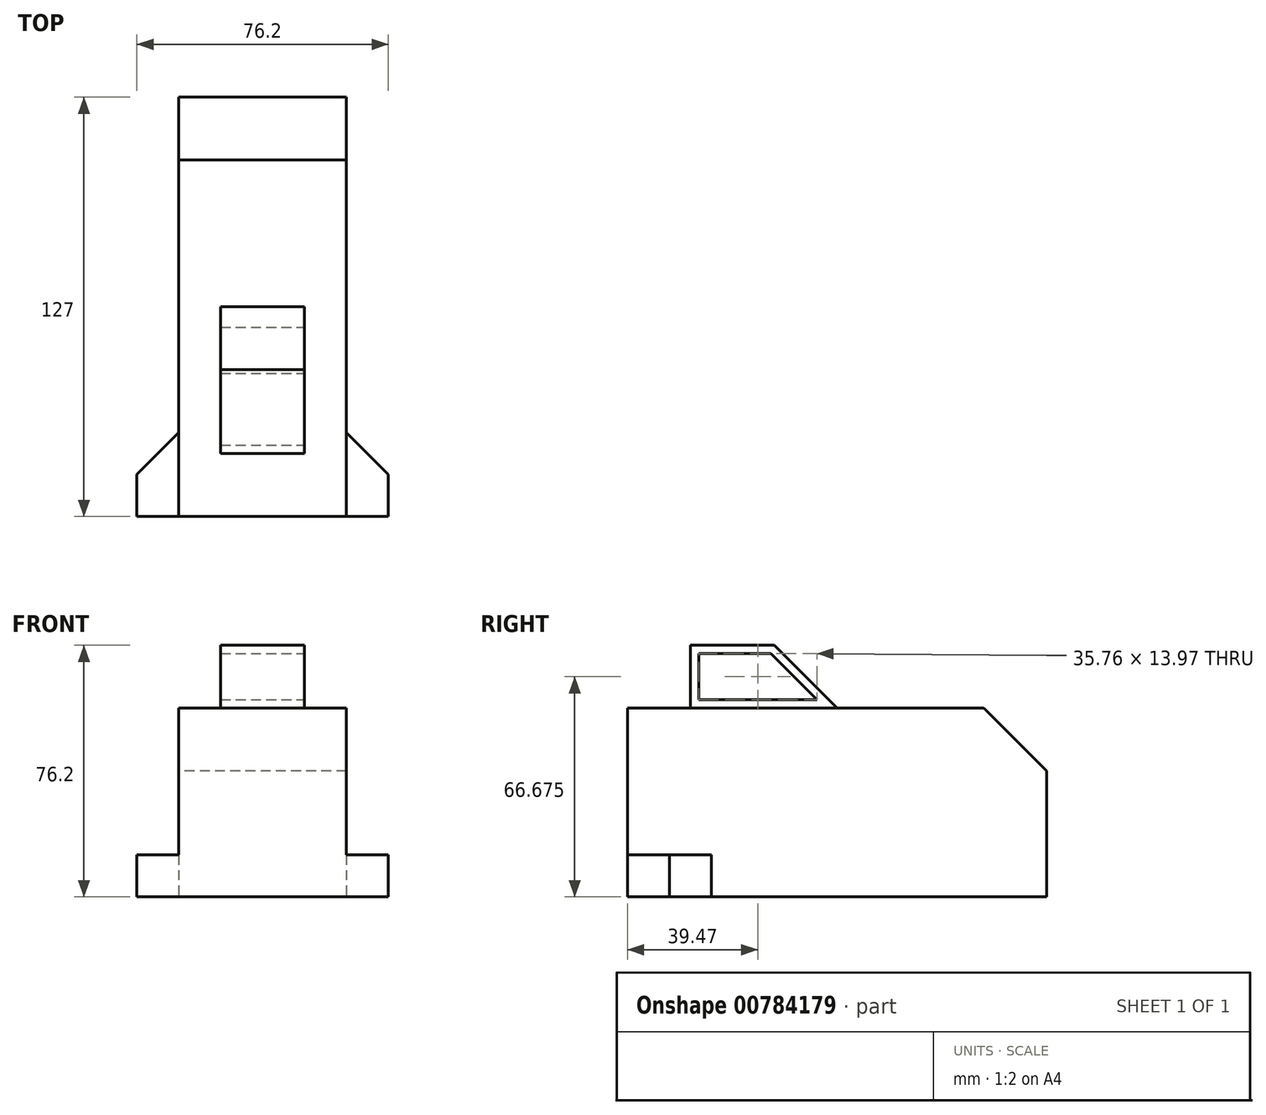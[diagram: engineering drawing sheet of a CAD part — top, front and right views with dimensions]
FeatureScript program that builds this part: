
annotation { "Feature Type Name" : "Feature", "Feature Type Description" : "" }
export const myFeature = defineFeature(function(context is Context, id is Id, definition is map)
    precondition{}
    {
        {
            var Q0;
            Q0=qCreatedBy(makeId("Right.planeOp"),FACE);
            var sketch = newSketch(context, id + "F0", { "sketchPlane" : qUnion([Q0])});
            skLineSegment(sketch, "E0", {"start": v(0, 0) * mm, "end": v(127, 0) * mm});
            skLineSegment(sketch, "E1", {"start": v(127, 0) * mm, "end": v(127, 38.1) * mm});
            skLineSegment(sketch, "E2", {"start": v(0, 0) * mm, "end": v(0, 57.15) * mm});
            skLineSegment(sketch, "E3", {"start": v(0, 57.15) * mm, "end": v(107.95, 57.15) * mm});
            skLineSegment(sketch, "E4", {"start": v(107.95, 57.15) * mm, "end": v(127, 38.1) * mm});
            skLineSegment(sketch, "E5", {"start": v(0, 0) * mm, "end": v(0, 12.7) * mm});
            skLineSegment(sketch, "E6", {"start": v(0, 12.7) * mm, "end": v(25.4, 12.7) * mm});
            skLineSegment(sketch, "E7", {"start": v(25.4, 12.7) * mm, "end": v(25.4, 0) * mm});
            skLineSegment(sketch, "E8", {"start": v(0, 57.15) * mm, "end": v(19.05, 57.15) * mm});
            skLineSegment(sketch, "E9", {"start": v(19.05, 57.15) * mm, "end": v(19.05, 76.2) * mm});
            skLineSegment(sketch, "E10", {"start": v(19.05, 76.2) * mm, "end": v(44.45, 76.2) * mm});
            skLineSegment(sketch, "E11", {"start": v(63.5, 57.15) * mm, "end": v(44.45, 76.2) * mm});
            skSolve(sketch);
        }
        {
            var Q0;
            {var subQ4=sQuery(id+"F0.wireOp",EDGE,"E1");Q0=makeQuery(id+"F0.imprint","IMPRINT",FACE,{"disambiguationData":[TD([[makeQuery(id+"F0.imprint","IMPRINT",EDGE,{"derivedFrom":subQ4}),1.0]])]});}
            extrude(context, id + "F1", {"entities" : qUnion([Q0]), "flatOperationType" : FlatOperationType.REMOVE, "depth" : 25.4 * mm, "offsetDistance" : 25.4 * mm, "domain" : OperationDomain.MODEL});
        }
        {
            var Q0;
            {var subQ4=sQuery(id+"F0.wireOp",EDGE,"E6");Q0=makeQuery(id+"F0.imprint","IMPRINT",FACE,{"disambiguationData":[TD([[makeQuery(id+"F0.imprint","IMPRINT",EDGE,{"derivedFrom":subQ4}),-1.0]])]});}
            extrude(context, id + "F2", {"entities" : qUnion([Q0]), "operationType" : NewBodyOperationType.ADD, "flatOperationType" : FlatOperationType.REMOVE, "depth" : 38.1 * mm, "offsetDistance" : 25.4 * mm, "domain" : OperationDomain.MODEL});
        }
        {
            var Q0;
            {var subQ2=sQuery(id+"F0.wireOp",EDGE,"E9");Q0=makeQuery(id+"F0.imprint","IMPRINT",FACE,{"disambiguationData":[TD([[makeQuery(id+"F0.imprint","IMPRINT",EDGE,{"derivedFrom":subQ2}),-1.0]])]});}
            extrude(context, id + "F3", {"entities" : qUnion([Q0]), "operationType" : NewBodyOperationType.ADD, "flatOperationType" : FlatOperationType.REMOVE, "depth" : 12.7 * mm, "offsetDistance" : 25.4 * mm, "domain" : OperationDomain.MODEL});
        }
        {
            var Q0;
            Q0=makeQuery(id+"F2.opExtrude","SWEPT_FACE",FACE,{"disambiguationData":[OSD([sQuery(id+"F0.wireOp",EDGE,"E6")])]});
            var sketch = newSketch(context, id + "F4", { "sketchPlane" : qUnion([Q0])});
            skLineSegment(sketch, "E12", {"start": v(38.1, 12.7) * mm, "end": v(25.4, 25.4) * mm});
            skSolve(sketch);
        }
        {
            var Q0;
            {var subQ0=sQuery(id+"F4.wireOp",EDGE,"E12");Q0=makeQuery(id+"F4.imprint","IMPRINT",FACE,{"disambiguationData":[TD([[makeQuery(id+"F4.imprint","IMPRINT",EDGE,{"derivedFrom":subQ0}),-1.0]])]});}
            extrude(context, id + "F5", {"entities" : qUnion([Q0]), "operationType" : NewBodyOperationType.REMOVE, "flatOperationType" : FlatOperationType.REMOVE, "oppositeDirection" : true, "depth" : 12.7 * mm, "offsetDistance" : 25.4 * mm, "domain" : OperationDomain.MODEL});
        }
        {
            var Q0;
            Q0=makeQuery(id+"F3.opExtrude","CAP_FACE",FACE,{"disambiguationData":[OSD([sQuery(id+"F0.wireOp",EDGE,"E3"),sQuery(id+"F0.wireOp",EDGE,"E9"),sQuery(id+"F0.wireOp",EDGE,"E10"),sQuery(id+"F0.wireOp",EDGE,"E11")])],"isStart":false});
            var sketch = newSketch(context, id + "F6", { "sketchPlane" : qUnion([Q0])});
            skLineSegment(sketch, "E13", {"start": v(21.59, 73.66) * mm, "end": v(21.59, 59.7) * mm});
            skLineSegment(sketch, "E14", {"start": v(21.59, 59.7) * mm, "end": v(57.35, 59.7) * mm});
            skLineSegment(sketch, "E15", {"start": v(21.59, 73.66) * mm, "end": v(43.38, 73.66) * mm});
            skPoint(sketch, "E16.orphan", {"position": v(21.59, 57.15) * mm});
            skLineSegment(sketch, "E17", {"start": v(52.17, 64.87) * mm, "end": v(57.35, 59.7) * mm});
            skLineSegment(sketch, "E18", {"start": v(52.17, 64.87) * mm, "end": v(43.38, 73.66) * mm});
            skPoint(sketch, "E19.orphan", {"position": v(44.45, 73.66) * mm});
            skPoint(sketch, "E20.start.orphan", {"position": v(53.98, 66.68) * mm});
            skSolve(sketch);
        }
        {
            var Q0;
            Q0=makeQuery(id+"F6.imprint","IMPRINT",FACE,{"disambiguationData":[TD([[makeQuery(id+"F6.imprint","IMPRINT",EDGE,{"derivedFrom":sQuery(id+"F6.wireOp",EDGE,"E13")}),1.0]])]});
            extrude(context, id + "F7", {"entities" : qUnion([Q0]), "operationType" : NewBodyOperationType.REMOVE, "flatOperationType" : FlatOperationType.REMOVE, "oppositeDirection" : true, "depth" : 12.7 * mm, "offsetDistance" : 25.4 * mm, "domain" : OperationDomain.MODEL});
        }
        {
            var Q0;
            Q0=makeQuery(id+"F1.opExtrude","SWEPT_BODY",BODY,{"disambiguationData":[OSD([sQuery(id+"F0.wireOp",EDGE,"E0"),sQuery(id+"F0.wireOp",EDGE,"E1"),sQuery(id+"F0.wireOp",EDGE,"E2"),sQuery(id+"F0.wireOp",EDGE,"E3"),sQuery(id+"F0.wireOp",EDGE,"E4"),sQuery(id+"F0.wireOp",EDGE,"E6"),sQuery(id+"F0.wireOp",EDGE,"E7")])]});
            var Q1;
            Q1=qCreatedBy(makeId("Right.planeOp"),FACE);
            mirror(context, id + "F8", {"operationType" : NewBodyOperationType.ADD, "entities" : qUnion([Q0]), "mirrorPlane" : qUnion([Q1])});
        }
    });
